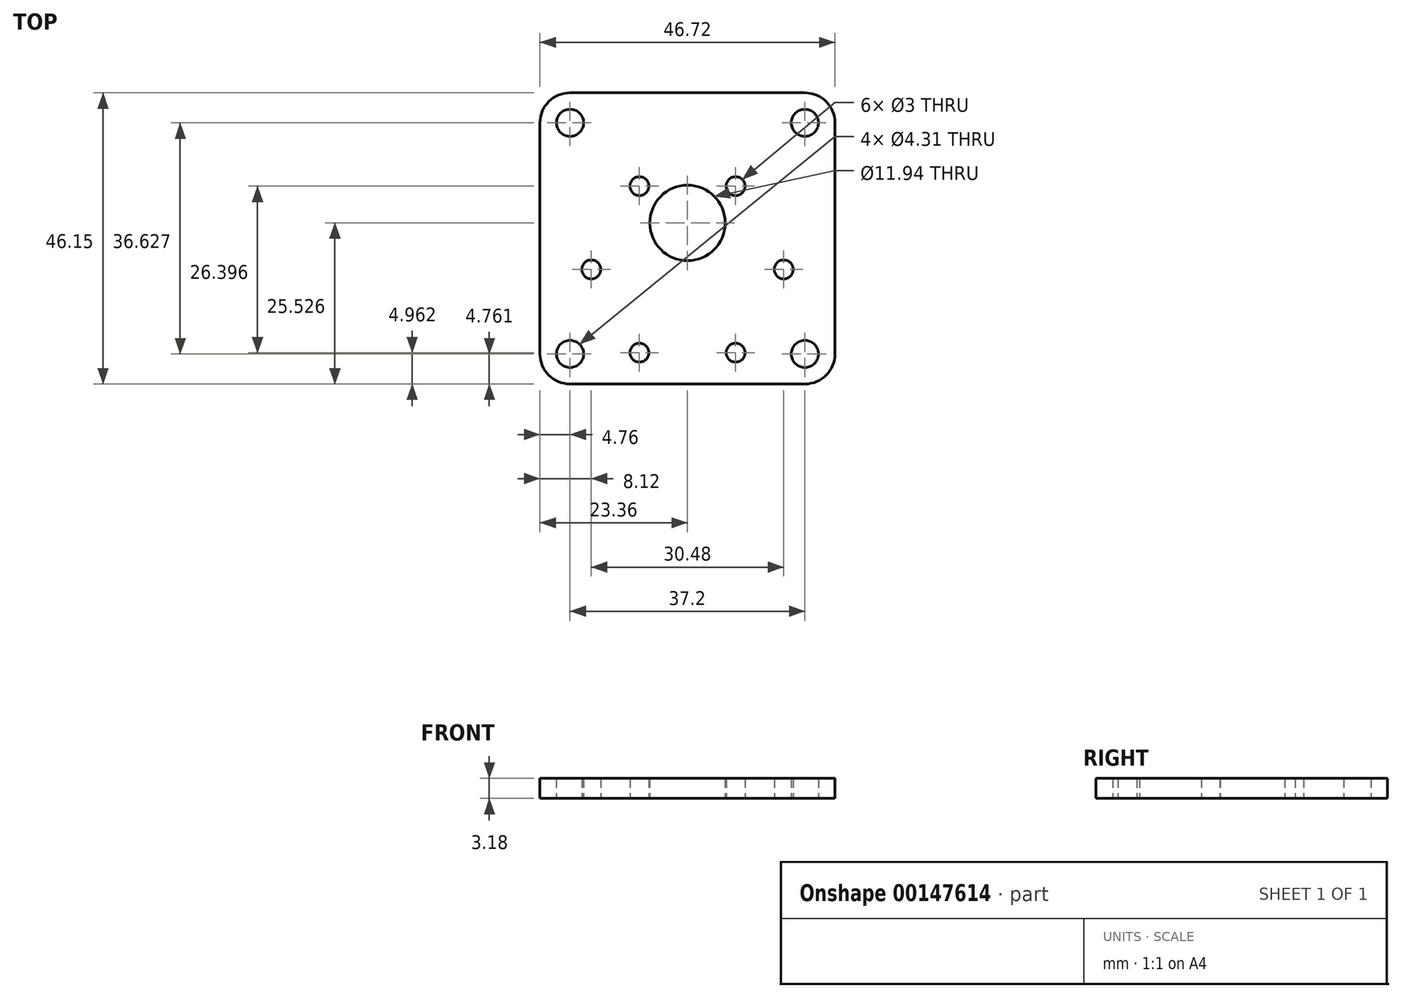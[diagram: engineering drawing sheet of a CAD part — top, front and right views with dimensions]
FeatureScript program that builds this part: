
annotation { "Feature Type Name" : "Feature", "Feature Type Description" : "" }
export const myFeature = defineFeature(function(context is Context, id is Id, definition is map)
    precondition{}
    {
        {
            var Q0;
            Q0=qCreatedBy(makeId("Top.planeOp"),FACE);
            var sketch = newSketch(context, id + "F0", { "sketchPlane" : qUnion([Q0])});
            skPoint(sketch, "E0.rect.middle", {"position": v(0, 0) * mm});
            skLineSegment(sketch, "E1", {"start": v(0, -7.37) * mm, "end": v(0, 7.37) * mm, "construction": true});
            skCircle(sketch, "E2.cCircle", {"center": v(0, 0) * mm, "radius": 13.2 * mm, "construction": true});
            skLineSegment(sketch, "E2.0", {"start": v(7.62, 13.2) * mm, "end": v(15.24, 0) * mm, "construction": true});
            skLineSegment(sketch, "E2.1", {"start": v(15.24, 0) * mm, "end": v(7.62, -13.2) * mm, "construction": true});
            skLineSegment(sketch, "E2.2", {"start": v(7.62, -13.2) * mm, "end": v(-7.62, -13.2) * mm, "construction": true});
            skLineSegment(sketch, "E2.3", {"start": v(-7.62, -13.2) * mm, "end": v(-15.24, 0) * mm, "construction": true});
            skLineSegment(sketch, "E2.4", {"start": v(-15.24, 0) * mm, "end": v(-7.62, 13.2) * mm, "construction": true});
            skLineSegment(sketch, "E2.5", {"start": v(-7.62, 13.2) * mm, "end": v(7.62, 13.2) * mm, "construction": true});
            skCircle(sketch, "E3", {"center": v(0, 0) * mm, "radius": 18.16 * mm, "construction": true});
            skCircle(sketch, "E4", {"center": v(7.62, 13.2) * mm, "radius": 2.92 * mm, "construction": true});
            skCircle(sketch, "E5", {"center": v(-7.62, 13.2) * mm, "radius": 1.5 * mm});
            skCircle(sketch, "E6", {"center": v(7.62, 13.2) * mm, "radius": 1.5 * mm});
            skCircle(sketch, "E7", {"center": v(15.24, 0) * mm, "radius": 1.5 * mm});
            skCircle(sketch, "E8", {"center": v(7.62, -13.2) * mm, "radius": 1.5 * mm});
            skCircle(sketch, "E9", {"center": v(-7.62, -13.2) * mm, "radius": 1.5 * mm});
            skCircle(sketch, "E10", {"center": v(-15.24, 0) * mm, "radius": 1.5 * mm});
            skCircle(sketch, "E11", {"center": v(0, 7.37) * mm, "radius": 5.97 * mm});
            skLineSegment(sketch, "E12", {"start": v(0, -7.37) * mm, "end": v(0, -18.16) * mm, "construction": true});
            skLineSegment(sketch, "E13.bottom", {"start": v(-23.36, -18.16) * mm, "end": v(23.36, -18.16) * mm});
            skLineSegment(sketch, "E13.top", {"start": v(-23.36, 28) * mm, "end": v(23.36, 28) * mm});
            skLineSegment(sketch, "E13.left", {"start": v(-23.36, -18.16) * mm, "end": v(-23.36, 28) * mm});
            skLineSegment(sketch, "E13.right", {"start": v(23.36, -18.16) * mm, "end": v(23.36, 28) * mm});
            skLineSegment(sketch, "E14.bottom", {"start": v(-18.6, -13.4) * mm, "end": v(18.6, -13.4) * mm, "construction": true});
            skLineSegment(sketch, "E14.top", {"start": v(-18.6, 23.23) * mm, "end": v(18.6, 23.23) * mm, "construction": true});
            skLineSegment(sketch, "E14.left", {"start": v(-18.6, -13.4) * mm, "end": v(-18.6, 23.23) * mm, "construction": true});
            skLineSegment(sketch, "E14.right", {"start": v(18.6, -13.4) * mm, "end": v(18.6, 23.23) * mm, "construction": true});
            skCircle(sketch, "E15", {"center": v(-18.6, -13.4) * mm, "radius": 4.76 * mm, "construction": true});
            skLineSegment(sketch, "E16", {"start": v(0, 23.23) * mm, "end": v(0, 28) * mm, "construction": true});
            skLineSegment(sketch, "E17", {"start": v(0, 23.23) * mm, "end": v(0, 7.37) * mm, "construction": true});
            skCircle(sketch, "E18", {"center": v(-18.6, 23.23) * mm, "radius": 2.15 * mm});
            skCircle(sketch, "E19", {"center": v(18.6, 23.23) * mm, "radius": 2.15 * mm});
            skCircle(sketch, "E20", {"center": v(-18.6, -13.4) * mm, "radius": 2.15 * mm});
            skCircle(sketch, "E21", {"center": v(18.6, -13.4) * mm, "radius": 2.15 * mm});
            skSolve(sketch);
        }
        {
            var Q0;
            Q0=qSketchRegion(id+"F0",true);
            extrude(context, id + "F1", {"entities" : qUnion([Q0]), "depth" : 3.17 * mm});
        }
        {
            var Q0;
            Q0=makeQuery(id+"F1.opExtrude","SWEPT_EDGE",EDGE,{"disambiguationData":[OSD([sQuery(id+"F0.wireOp",EDGE,"E13.bottom"),sQuery(id+"F0.wireOp",EDGE,"E13.left")])]});
            var Q1;
            Q1=makeQuery(id+"F1.opExtrude","SWEPT_EDGE",EDGE,{"disambiguationData":[OSD([sQuery(id+"F0.wireOp",EDGE,"E13.bottom"),sQuery(id+"F0.wireOp",EDGE,"E13.right")])]});
            var Q2;
            Q2=makeQuery(id+"F1.opExtrude","SWEPT_EDGE",EDGE,{"disambiguationData":[OSD([sQuery(id+"F0.wireOp",EDGE,"E13.top"),sQuery(id+"F0.wireOp",EDGE,"E13.right")])]});
            var Q3;
            Q3=makeQuery(id+"F1.opExtrude","SWEPT_EDGE",EDGE,{"disambiguationData":[OSD([sQuery(id+"F0.wireOp",EDGE,"E13.top"),sQuery(id+"F0.wireOp",EDGE,"E13.left")])]});
            fillet(context, id + "F2", {"entities" : qUnion([Q0, Q1, Q2, Q3]), "radius" : 4.76 * mm, "tangentPropagation" : true, "allowEdgeOverflow" : false});
        }
    });
